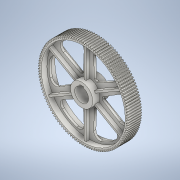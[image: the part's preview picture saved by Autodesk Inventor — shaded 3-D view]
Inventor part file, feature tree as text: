
AUTODESK INVENTOR PART (.ipt)
format: ipt  version: 2020 (Build 240168000, 168)  size: 1,211,904 bytes
history: native  units: mm (DEFAULTED — no unit token found)
features: sketch x8, extrude x7, plane x5, other x5, pattern_circular x2, loft x1, projected_geometry x1
ambient origin geometry x8: Origin, YZ Plane, XZ Plane, XY Plane, X Axis, Y Axis, Z Axis, Center Point
bodies: Solid1 (feature_tree), 实体2 (feature_tree)
feature tree (29):
  extrude  "Extrusion1"  Depth=73.0mm TaperAngle=0.0deg
  plane  "Work Plane2"
  plane  "Work Plane8"
  plane  "Work Plane9"
  other  "正齿轮"
  sketch  "草图3"  dims[d16=276.0mm d17=0.0mm d34=0.263999mm]
  extrude  "拉伸2"  Depth=10.0mm TaperAngle=0.0deg
  extrude  "拉伸9"  Depth=0.263999mm TaperAngle=0.0deg
  plane  "工作平面11"
  sketch  "草图5"  dims[d39=0.0mm d41=0.0mm]
  extrude  "拉伸4"  TaperAngle=0.0deg  [1 undecoded]
  plane  "工作平面12"
  loft  "放样1"
  extrude  "拉伸5"  Depth=75.0mm
  other  "合并1"
  pattern_circular  "环形阵列1"  Count=12  [1 undecoded]
  extrude  "拉伸10"  Depth=20.0mm
  extrude  "拉伸11"  Depth=5.0mm
  pattern_circular  "环形阵列3"  [2 undecoded]
  sketch  "Sketch1"  dims[d0=484.0mm d1=73.0mm d2=0.0mm]
  sketch  "Sketch2"  dims[d3=476.0mm d4=10.0mm d5=0.0mm]
  other  "Srf1"
  projected_geometry  "投影回路1"
  sketch  "草图6"  dims[d43=276.0mm d46=276.0mm]
  sketch  "草图7"  dims[d47=0.0mm d48=0.0mm d49=75.0mm d50=120.0mm]
  sketch  "草图8"  dims[d51=8.5mm d52=0.0mm d53=20.0mm]
  sketch  "草图9"  dims[d54=12.0mm d55=5.0mm d56=81.5mm d57=0.0mm d68=59.0mm d69=10.0mm d70=53.0mm d71=12.0mm d72=60.0mm d73=476.0mm d74=452.0mm d75=0.0mm d76=0.0mm d77=227.0mm d78=12.0mm d79=48.0mm d80=10.0mm d81=53.0mm d82=36.5mm d83=0.0mm d84=90.0deg d85=0.0mm d86=90.0deg d87=10.0mm d88=0.0mm d89=20.0mm d91=90.0deg d99=10.0mm d100=0.0mm d101=60.0mm d102=360.0deg d104=10.0mm d105=0.0mm d109=428.0mm d110=144.0mm d111=60.0mm d112=60.0mm d114=10.0mm d115=10.0mm d116=10.0mm d117=0.0mm d118=60.0mm d119=360.0deg d113=0.5mm]
  other  "投影剖切边1"
  other  "投影剖切边2"
note: 4 required parameter values undecoded (feature->parameter linkage not recoverable at this tier; creation-order binding heuristic only, values carry confidence <= 0.55)
